# Revit family: Баум
name_source: partatom
category: Осветительные приборы
units: mm (PartAtom-declared; Revit-internal decimal feet)

## family parameters
Всегда вертикально = Да
Источник света = Да
На основе рабочей плоскости = Нет
Общий = Нет
При загрузке вырезать с полостями = Нет
Размер круглого соединителя = Использовать диаметр
Тип детали = Нормальный
Точка расчета площади = Нет

## types (2) — shared parameters
ADSK_URL страницы изделия = https://www.allfresco.ru
ADSK_Единица измерения = шт.
ADSK_Завод-изготовитель = ALFRESCO
ADSK_Количество фаз = 2
ADSK_Модель = Баум ДТУ-96-AF
ADSK_Напряжение = 220 В
ADSK_Полная мощность = 0 В·А
ADSK_Ток = 0 А
ADSK_Энергоэффективность = 100 лм/Вт
IP Class = IP 67
L_столб верх = 100 мм
L_столб низ = 95 мм
L_фланец = 150 мм
L_фланец отверстия = 120 мм
S_столб верх = 100 мм
S_столб низ = 95 мм
S_фланец = 150 мм
S_фланец отверстия = 120 мм
S_шапка = 3 мм
X1_отступ стекла = 18 мм
X_отступ стекла = 53 мм
d_фланец отверстия = 12 мм
h1_окно = 28 мм
h_окно = 300 мм
h_опуск шапки = 21 мм
h_пластина = 5 мм
h_рассеиватель = 5 мм
h_светильник = 146 мм
h_столб = 3000 мм
h_фланец = 4 мм
h_шапка = 29 мм
r светильник = 445 мм
r_закругления = 1 мм
r_пластина = 50 мм
r_рассеиватель = 440 мм
r_столб = 30 мм
Блок аварийного питания = Нет
Класс защиты = 1
Класс пожароопасности = F (светильники предназначены для установки непосредственно на поверхность из нормально воспламеняемых материалов)
Климатическая зона = УХЛ1
Корпус светильника = Антрацит
Материал рассеивателя = -
Область использования = Парки, скверы, общественные пространства, городская инфраструктура
Полная установленная мощность = 0 В·А
Рассеиватель = Материал рассеивателя
Светофильтр = 16777215
Смещение цветовой температуры при затухании лампы = <Нет>
Стекло = Стекло
Столб = Ясень
Таблица выбора = Таблица параметров светильников
Температура эксплуатации = -40 +50
Тип ИС = LED-модуль
Тип КСС = Специальная
Тип ПРА = -
Тип продукции = LED-светильник
Угол наклона = 90.00°
Цветоывая температура = 2700-5500
zero-valued in all types: ADSK_Количество фаз числовое, ADSK_Коэффициент мощности

## per-type parameters (varying)
| type | ADSK_Артикул | ADSK_Масса | ADSK_Масса_Текст | ADSK_Наименование | ADSK_Номинальная мощность | ADSK_Размер_Высота | ADSK_Фактическая мощность | h_столб верх | h_столб низ | Файл фотометрической сетки |
| ДТУ962 Светодиодный светильник Баум ДТУ-96-AF-6Вт-1,0 | ДТУ962 | 11 | 11 | ДТУ962 Светодиодный светильник Баум ДТУ-96-AF-6Вт-1.0 | 6 Вт | 1000 мм | 6 Вт | 800 мм | 202 мм | DTU-96-AF Baum 6 W.ies |
| ДТУ961 Светодиодный светильник Баум ДТУ-96-AF-4Вт-0,6 | ДТУ961 | 7 | 7 | ДТУ961 Светодиодный светильник Баум ДТУ-96-AF-4Вт-0.6 | 4 Вт | 600 мм | 4 Вт | 400 мм | 102 мм | DTU-96-AF Baum 4 W .ies |
